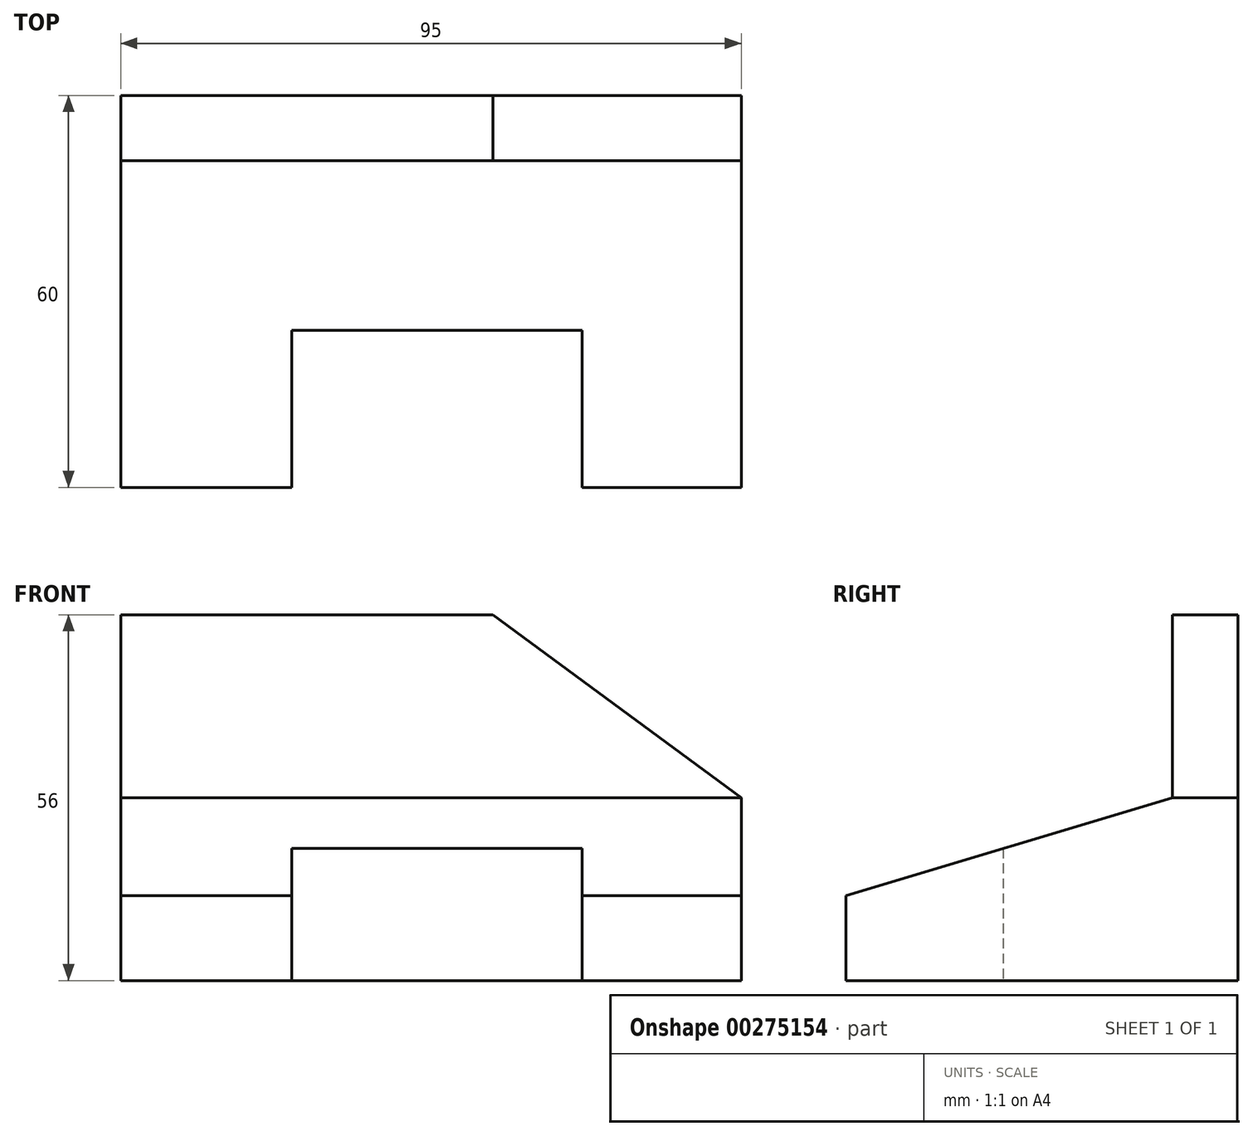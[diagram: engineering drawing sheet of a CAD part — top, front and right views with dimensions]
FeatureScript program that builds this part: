
annotation { "Feature Type Name" : "Feature", "Feature Type Description" : "" }
export const myFeature = defineFeature(function(context is Context, id is Id, definition is map)
    precondition{}
    {
        {
            var Q0;
            Q0=qCreatedBy(makeId("Right.planeOp"),FACE);
            var sketch = newSketch(context, id + "F0", { "sketchPlane" : qUnion([Q0])});
            skLineSegment(sketch, "E0", {"start": v(0, 0) * mm, "end": v(0, 56) * mm});
            skLineSegment(sketch, "E1", {"start": v(0, 56) * mm, "end": v(-10, 56) * mm});
            skLineSegment(sketch, "E2", {"start": v(-10, 56) * mm, "end": v(-10, 28) * mm});
            skLineSegment(sketch, "E3", {"start": v(-10, 28) * mm, "end": v(-60, 13) * mm});
            skLineSegment(sketch, "E4", {"start": v(-60, 13) * mm, "end": v(-60, 0) * mm});
            skLineSegment(sketch, "E5", {"start": v(-60, 0) * mm, "end": v(0, 0) * mm});
            skSolve(sketch);
        }
        {
            var Q0;
            Q0=makeQuery(id+"F0.imprint","IMPRINT",FACE,{"disambiguationData":[TD([[makeQuery(id+"F0.imprint","IMPRINT",EDGE,{"derivedFrom":sQuery(id+"F0.wireOp",EDGE,"E0")}),1.0]])]});
            extrude(context, id + "F1", {"entities" : qUnion([Q0]), "depth" : 95 * mm});
        }
        {
            var Q0;
            Q0=makeQuery(id+"F1.opExtrude","SWEPT_FACE",FACE,{"disambiguationData":[OSD([sQuery(id+"F0.wireOp",EDGE,"E2")])]});
            var sketch = newSketch(context, id + "F2", { "sketchPlane" : qUnion([Q0])});
            skLineSegment(sketch, "E6", {"start": v(57, 56) * mm, "end": v(95, 28) * mm});
            skSolve(sketch);
        }
        {
            var Q0;
            {var subQ0=sQuery(id+"F2.wireOp",EDGE,"E6");Q0=makeQuery(id+"F2.imprint","IMPRINT",FACE,{"disambiguationData":[TD([[makeQuery(id+"F2.imprint","IMPRINT",EDGE,{"derivedFrom":subQ0}),1.0]])]});}
            var Q1;
            Q1=makeQuery(id+"F1.opExtrude","SWEPT_FACE",FACE,{"disambiguationData":[OSD([sQuery(id+"F0.wireOp",EDGE,"E0")])]});
            extrude(context, id + "F3", {"entities" : qUnion([Q0]), "operationType" : NewBodyOperationType.REMOVE, "endBound" : BoundingType.THROUGH_ALL, "oppositeDirection" : true, "endBoundEntityFace" : qUnion([Q1]), "depth" : 25 * mm});
        }
        {
            var Q0;
            Q0=makeQuery(id+"F1.opExtrude","SWEPT_FACE",FACE,{"disambiguationData":[OSD([sQuery(id+"F0.wireOp",EDGE,"E5")])]});
            var sketch = newSketch(context, id + "F4", { "sketchPlane" : qUnion([Q0])});
            skLineSegment(sketch, "E7.bottom", {"start": v(26.15, 60) * mm, "end": v(70.6, 60) * mm});
            skLineSegment(sketch, "E7.top", {"start": v(26.15, 35.93) * mm, "end": v(70.6, 35.93) * mm});
            skLineSegment(sketch, "E7.left", {"start": v(26.15, 60) * mm, "end": v(26.15, 35.93) * mm});
            skLineSegment(sketch, "E7.right", {"start": v(70.6, 60) * mm, "end": v(70.6, 35.93) * mm});
            skSolve(sketch);
        }
        {
            var Q0;
            Q0 = qSketchRegion(id + "F4", true);
            extrude(context, id + "F5", {"entities" : qUnion([Q0]), "operationType" : NewBodyOperationType.REMOVE, "oppositeDirection" : true, "depth" : 61.3 * mm});
        }
    });
